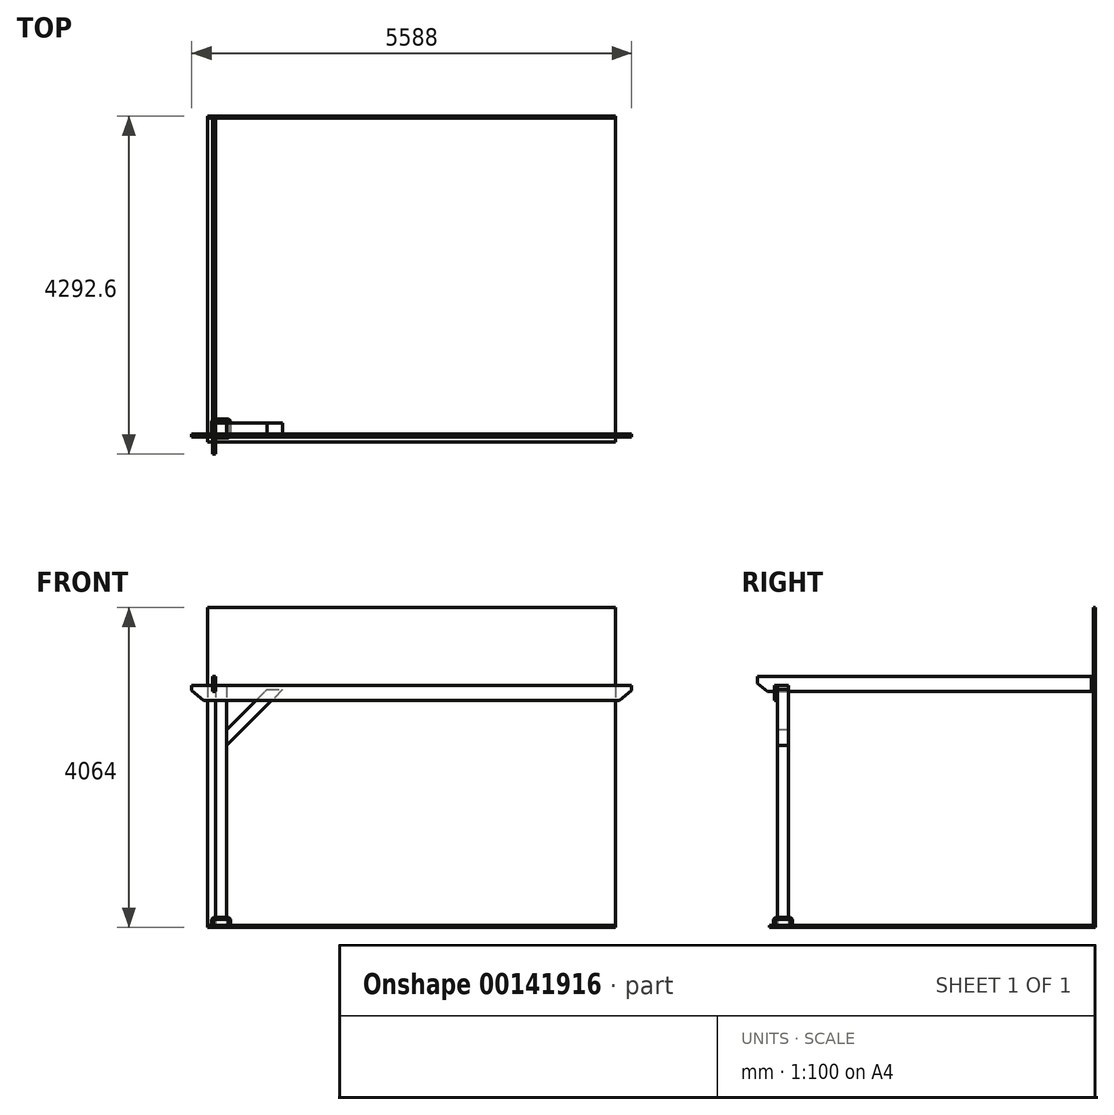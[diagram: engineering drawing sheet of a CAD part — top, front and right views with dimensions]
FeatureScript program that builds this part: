
annotation { "Feature Type Name" : "Feature", "Feature Type Description" : "" }
export const myFeature = defineFeature(function(context is Context, id is Id, definition is map)
    precondition{}
    {
        {
            var Q0;
            Q0=qCreatedBy(makeId("Top.planeOp"),FACE);
            var sketch = newSketch(context, id + "F0", { "sketchPlane" : qUnion([Q0])});
            skLineSegment(sketch, "E0.bottom", {"start": v(2590.8, 2057.4) * mm, "end": v(-2590.8, 2057.4) * mm});
            skLineSegment(sketch, "E0.top", {"start": v(2590.8, -2057.4) * mm, "end": v(-2590.8, -2057.4) * mm});
            skLineSegment(sketch, "E0.left", {"start": v(2590.8, 2057.4) * mm, "end": v(2590.8, -2057.4) * mm});
            skLineSegment(sketch, "E0.right", {"start": v(-2590.8, 2057.4) * mm, "end": v(-2590.8, -2057.4) * mm});
            skPoint(sketch, "E0.middle", {"position": v(0, 0) * mm});
            skSolve(sketch);
        }
        {
            var Q0;
            Q0=makeQuery(id+"F0.imprint","IMPRINT",FACE,{"disambiguationData":[TD([[makeQuery(id+"F0.imprint","IMPRINT",EDGE,{"derivedFrom":sQuery(id+"F0.wireOp",EDGE,"E0.bottom")}),1.0]])]});
            extrude(context, id + "F1", {"entities" : qUnion([Q0]), "depth" : 25.4 * mm});
        }
        {
            var Q0;
            Q0=makeQuery(id+"F1.opExtrude","SWEPT_FACE",FACE,{"disambiguationData":[OSD([sQuery(id+"F0.wireOp",EDGE,"E0.right")])]});
            var sketch = newSketch(context, id + "F2", { "sketchPlane" : qUnion([Q0])});
            skLineSegment(sketch, "E1.bottom", {"start": v(-2057.4, 0) * mm, "end": v(-2082.8, 0) * mm});
            skLineSegment(sketch, "E1.top", {"start": v(-2057.4, 4064) * mm, "end": v(-2082.8, 4064) * mm});
            skLineSegment(sketch, "E1.left", {"start": v(-2057.4, 0) * mm, "end": v(-2057.4, 4064) * mm});
            skLineSegment(sketch, "E1.right", {"start": v(-2082.8, 0) * mm, "end": v(-2082.8, 4064) * mm});
            skSolve(sketch);
        }
        {
            var Q0;
            Q0 = qSketchRegion(id + "F2", true);
            var Q1;
            Q1=makeQuery(id+"F1.opExtrude","SWEPT_FACE",FACE,{"disambiguationData":[OSD([sQuery(id+"F0.wireOp",EDGE,"E0.left")])]});
            extrude(context, id + "F3", {"entities" : qUnion([Q0]), "endBound" : BoundingType.UP_TO_SURFACE, "oppositeDirection" : true, "endBoundEntityFace" : qUnion([Q1]), "depth" : 25.4 * mm});
        }
        {
            var Q0;
            Q0=makeQuery(id+"F1.opExtrude","CAP_FACE",FACE,{"disambiguationData":[OSD([sQuery(id+"F0.wireOp",EDGE,"E0.bottom"),sQuery(id+"F0.wireOp",EDGE,"E0.top"),sQuery(id+"F0.wireOp",EDGE,"E0.left"),sQuery(id+"F0.wireOp",EDGE,"E0.right")])],"isStart":false});
            var sketch = newSketch(context, id + "F4", { "sketchPlane" : qUnion([Q0])});
            skLineSegment(sketch, "E2.bottom", {"start": v(-2489.2, -1816.1) * mm, "end": v(-2349.5, -1816.1) * mm});
            skLineSegment(sketch, "E2.top", {"start": v(-2489.2, -1955.8) * mm, "end": v(-2349.5, -1955.8) * mm});
            skLineSegment(sketch, "E2.left", {"start": v(-2489.2, -1816.1) * mm, "end": v(-2489.2, -1955.8) * mm});
            skLineSegment(sketch, "E2.right", {"start": v(-2349.5, -1816.1) * mm, "end": v(-2349.5, -1955.8) * mm});
            skSolve(sketch);
        }
        {
            var Q0;
            Q0 = qSketchRegion(id + "F4", true);
            extrude(context, id + "F5", {"entities" : qUnion([Q0]), "depth" : 3048 * mm});
        }
        {
            var Q0;
            Q0=makeQuery(id+"F5.opExtrude","SWEPT_FACE",FACE,{"disambiguationData":[OSD([sQuery(id+"F4.wireOp",EDGE,"E2.top")])]});
            var sketch = newSketch(context, id + "F6", { "sketchPlane" : qUnion([Q0])});
            skLineSegment(sketch, "E3.bottom", {"start": v(-2794, 3073.4) * mm, "end": v(2794, 3073.4) * mm});
            skLineSegment(sketch, "E3.top", {"start": v(-2794, 2882.9) * mm, "end": v(2794, 2882.9) * mm});
            skLineSegment(sketch, "E3.left", {"start": v(-2794, 3073.4) * mm, "end": v(-2794, 2882.9) * mm});
            skLineSegment(sketch, "E3.right", {"start": v(2794, 3073.4) * mm, "end": v(2794, 2882.9) * mm});
            skSolve(sketch);
        }
        {
            var Q0;
            Q0 = qSketchRegion(id + "F6", true);
            extrude(context, id + "F7", {"entities" : qUnion([Q0]), "depth" : 38.1 * mm});
        }
        {
            var Q0;
            Q0=makeQuery(id+"F7.opExtrude","SWEPT_EDGE",EDGE,{"disambiguationData":[OSD([sQuery(id+"F6.wireOp",EDGE,"E3.top"),sQuery(id+"F6.wireOp",EDGE,"E3.left")])]});
            var Q1;
            Q1=makeQuery(id+"F7.opExtrude","SWEPT_EDGE",EDGE,{"disambiguationData":[OSD([sQuery(id+"F6.wireOp",EDGE,"E3.top"),sQuery(id+"F6.wireOp",EDGE,"E3.right")])]});
            chamfer(context, id + "F8", {"entities" : qUnion([Q0, Q1]), "chamferType" : ChamferType.TWO_OFFSETS, "width1" : 152.4 * mm, "oppositeDirection" : false, "width2" : 127 * mm, "tangentPropagation" : true});
        }
        {
            var Q0;
            Q0=makeQuery(id+"F5.opExtrude","SWEPT_FACE",FACE,{"disambiguationData":[OSD([sQuery(id+"F4.wireOp",EDGE,"E2.left")])]});
            var sketch = newSketch(context, id + "F9", { "sketchPlane" : qUnion([Q0])});
            skLineSegment(sketch, "E4.bottom", {"start": v(2209.8, 3187.7) * mm, "end": v(-2032, 3187.7) * mm});
            skLineSegment(sketch, "E4.top", {"start": v(2209.8, 2997.2) * mm, "end": v(-2032, 2997.2) * mm});
            skLineSegment(sketch, "E4.left", {"start": v(2209.8, 3187.7) * mm, "end": v(2209.8, 2997.2) * mm});
            skLineSegment(sketch, "E4.right", {"start": v(-2032, 3187.7) * mm, "end": v(-2032, 2997.2) * mm});
            skSolve(sketch);
        }
        {
            var Q0;
            Q0 = qSketchRegion(id + "F9", true);
            extrude(context, id + "F10", {"entities" : qUnion([Q0]), "depth" : 38.1 * mm});
        }
        {
            var Q0;
            Q0=makeQuery(id+"F10.opExtrude","SWEPT_EDGE",EDGE,{"disambiguationData":[OSD([sQuery(id+"F9.wireOp",EDGE,"E4.top"),sQuery(id+"F9.wireOp",EDGE,"E4.left")])]});
            chamfer(context, id + "F11", {"entities" : qUnion([Q0]), "chamferType" : ChamferType.TWO_OFFSETS, "width1" : 101.6 * mm, "oppositeDirection" : false, "width2" : 127 * mm, "tangentPropagation" : true});
        }
        {
            var Q0;
            Q0=makeQuery(id+"F5.opExtrude","SWEPT_FACE",FACE,{"disambiguationData":[OSD([sQuery(id+"F4.wireOp",EDGE,"E2.top")])]});
            var sketch = newSketch(context, id + "F12", { "sketchPlane" : qUnion([Q0])});
            skLineSegment(sketch, "E5", {"start": v(-2349.5, 2508.97) * mm, "end": v(-1835.87, 3022.6) * mm});
            skLineSegment(sketch, "E6", {"start": v(-1835.87, 3022.6) * mm, "end": v(-1638.3, 3022.6) * mm});
            skLineSegment(sketch, "E7", {"start": v(-1638.3, 3022.6) * mm, "end": v(-2349.5, 2311.4) * mm});
            skLineSegment(sketch, "E8", {"start": v(-2349.5, 2311.4) * mm, "end": v(-2349.5, 2508.97) * mm});
            skSolve(sketch);
        }
        {
            var Q0;
            Q0 = qSketchRegion(id + "F12", true);
            extrude(context, id + "F13", {"entities" : qUnion([Q0]), "oppositeDirection" : true, "depth" : 139.7 * mm});
        }
        {
            var Q0;
            Q0=makeQuery(id+"F1.opExtrude","CAP_FACE",FACE,{"disambiguationData":[OSD([sQuery(id+"F0.wireOp",EDGE,"E0.bottom"),sQuery(id+"F0.wireOp",EDGE,"E0.top"),sQuery(id+"F0.wireOp",EDGE,"E0.left"),sQuery(id+"F0.wireOp",EDGE,"E0.right")])],"isStart":false});
            var sketch = newSketch(context, id + "F14", { "sketchPlane" : qUnion([Q0])});
            skLineSegment(sketch, "E9.bottom", {"start": v(-2540, -2006.6) * mm, "end": v(-2298.7, -2006.6) * mm});
            skLineSegment(sketch, "E9.top", {"start": v(-2540, -1765.3) * mm, "end": v(-2298.7, -1765.3) * mm});
            skLineSegment(sketch, "E9.left", {"start": v(-2540, -2006.6) * mm, "end": v(-2540, -1765.3) * mm});
            skLineSegment(sketch, "E9.right", {"start": v(-2298.7, -2006.6) * mm, "end": v(-2298.7, -1765.3) * mm});
            skSolve(sketch);
        }
        {
            var Q0;
            Q0 = qSketchRegion(id + "F14", true);
            extrude(context, id + "F15", {"entities" : qUnion([Q0]), "depth" : 101.6 * mm});
        }
        {
            var Q0;
            Q0=makeQuery(id+"F15.opExtrude","SWEPT_EDGE",EDGE,{"disambiguationData":[OSD([sQuery(id+"F14.wireOp",EDGE,"E9.bottom"),sQuery(id+"F14.wireOp",EDGE,"E9.left")])]});
            var Q1;
            Q1=makeQuery(id+"F15.opExtrude","SWEPT_EDGE",EDGE,{"disambiguationData":[OSD([sQuery(id+"F14.wireOp",EDGE,"E9.top"),sQuery(id+"F14.wireOp",EDGE,"E9.left")])]});
            var Q2;
            Q2=makeQuery(id+"F15.opExtrude","SWEPT_EDGE",EDGE,{"disambiguationData":[OSD([sQuery(id+"F14.wireOp",EDGE,"E9.bottom"),sQuery(id+"F14.wireOp",EDGE,"E9.right")])]});
            var Q3;
            Q3=makeQuery(id+"F15.opExtrude","SWEPT_EDGE",EDGE,{"disambiguationData":[OSD([sQuery(id+"F14.wireOp",EDGE,"E9.top"),sQuery(id+"F14.wireOp",EDGE,"E9.right")])]});
            chamfer(context, id + "F16", {"entities" : qUnion([Q0, Q1, Q2, Q3]), "width" : 25.4 * mm, "tangentPropagation" : true});
        }
        {
            var Q0;
            Q0=makeQuery(id+"F15.opExtrude","CAP_EDGE",EDGE,{"disambiguationData":[OSD([sQuery(id+"F14.wireOp",EDGE,"E9.left")])],"isStart":false});
            var Q1;
            Q1=makeQuery(id+"F15.opExtrude","CAP_EDGE",EDGE,{"disambiguationData":[OSD([sQuery(id+"F14.wireOp",EDGE,"E9.bottom")])],"isStart":false});
            var Q2;
            Q2=makeQuery(id+"F15.opExtrude","CAP_EDGE",EDGE,{"disambiguationData":[OSD([sQuery(id+"F14.wireOp",EDGE,"E9.right")])],"isStart":false});
            var Q3;
            Q3=makeQuery(id+"F15.opExtrude","CAP_EDGE",EDGE,{"disambiguationData":[OSD([sQuery(id+"F14.wireOp",EDGE,"E9.top")])],"isStart":false});
            chamfer(context, id + "F17", {"entities" : qUnion([Q0, Q1, Q2, Q3]), "width" : 25.4 * mm, "tangentPropagation" : true});
        }
    });
